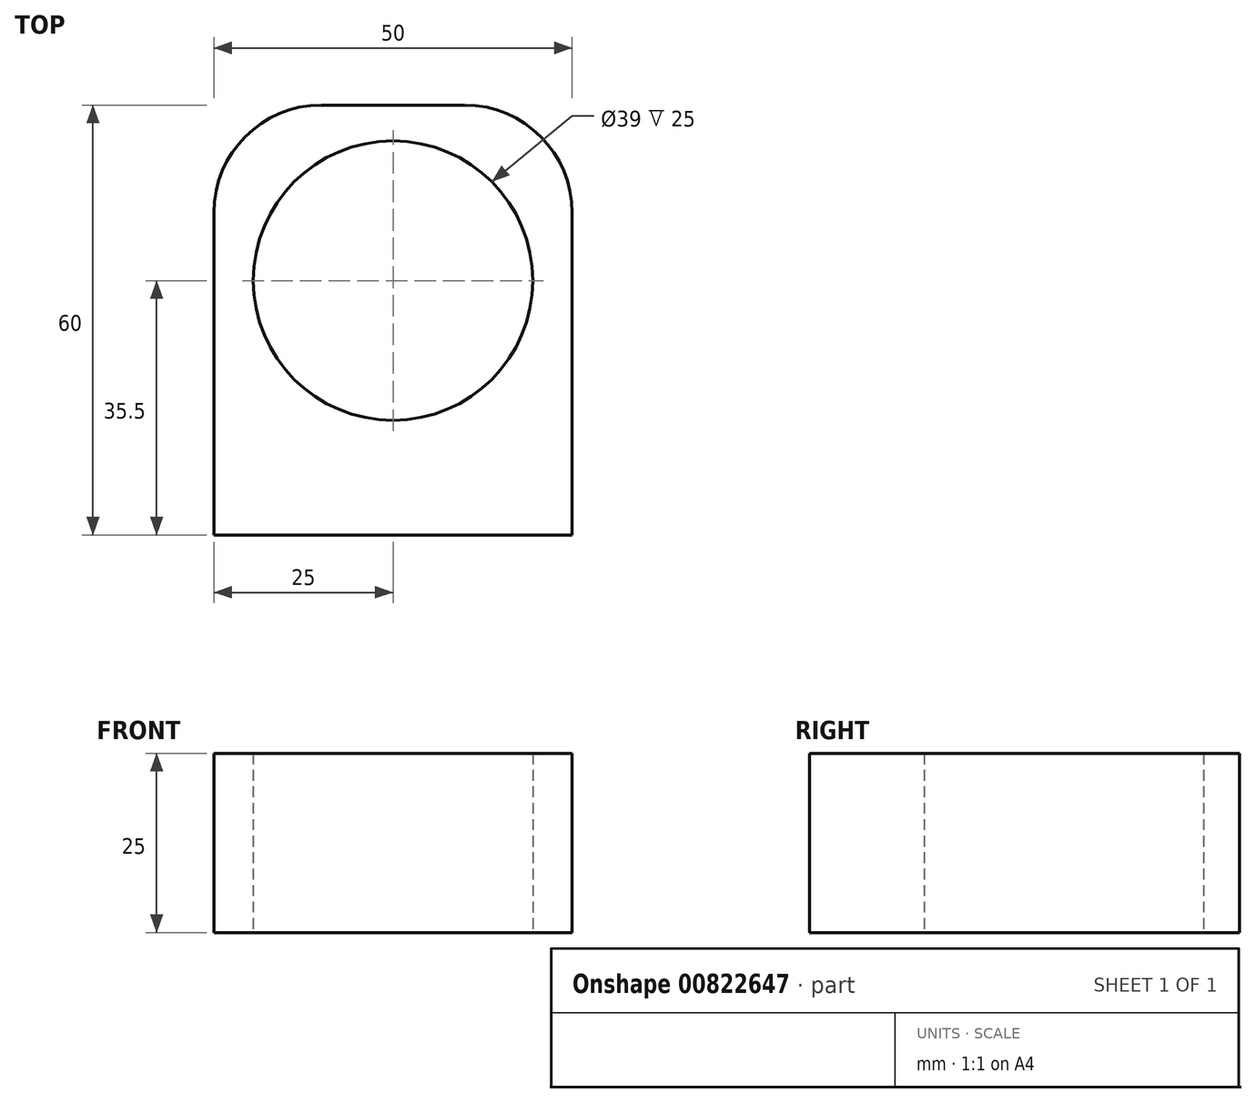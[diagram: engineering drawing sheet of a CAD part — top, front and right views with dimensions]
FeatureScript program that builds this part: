
annotation { "Feature Type Name" : "Feature", "Feature Type Description" : "" }
export const myFeature = defineFeature(function(context is Context, id is Id, definition is map)
    precondition{}
    {
        {
            var Q0;
            Q0=qCreatedBy(makeId("Top.planeOp"),FACE);
            var sketch = newSketch(context, id + "F0", { "sketchPlane" : qUnion([Q0])});
            skLineSegment(sketch, "E0.bottom", {"start": v(25, -30) * mm, "end": v(-25, -30) * mm});
            skLineSegment(sketch, "E0.top", {"start": v(25, 30) * mm, "end": v(-25, 30) * mm});
            skLineSegment(sketch, "E0.left", {"start": v(25, -30) * mm, "end": v(25, 30) * mm});
            skLineSegment(sketch, "E0.right", {"start": v(-25, -30) * mm, "end": v(-25, 30) * mm});
            skPoint(sketch, "E0.middle", {"position": v(0, 0) * mm});
            skPoint(sketch, "E1", {"position": v(0, 5.5) * mm});
            skCircle(sketch, "E2", {"center": v(0, 5.5) * mm, "radius": 19.5 * mm});
            skSolve(sketch);
        }
        {
            var Q0;
            Q0=makeQuery(id+"F0.imprint","IMPRINT",FACE,{"disambiguationData":[TD([[makeQuery(id+"F0.imprint","IMPRINT",EDGE,{"derivedFrom":sQuery(id+"F0.wireOp",EDGE,"E0.bottom")}),-1.0]])]});
            extrude(context, id + "F1", {"entities" : qUnion([Q0]), "depth" : 25 * mm, "offsetDistance" : 25 * mm});
        }
        {
            var Q0;
            Q0=makeQuery(id+"F1.opExtrude","SWEPT_EDGE",EDGE,{"disambiguationData":[OSD([sQuery(id+"F0.wireOp",EDGE,"E0.top"),sQuery(id+"F0.wireOp",EDGE,"E0.right")])]});
            fillet(context, id + "F2", {"entities" : qUnion([Q0]), "radius" : 15 * mm, "tangentPropagation" : true, "allowEdgeOverflow" : false});
        }
        {
            var Q0;
            Q0=makeQuery(id+"F1.opExtrude","SWEPT_EDGE",EDGE,{"disambiguationData":[OSD([sQuery(id+"F0.wireOp",EDGE,"E0.top"),sQuery(id+"F0.wireOp",EDGE,"E0.right")])]});
            var Q1;
            Q1=makeQuery(id+"F1.opExtrude","SWEPT_EDGE",EDGE,{"disambiguationData":[OSD([sQuery(id+"F0.wireOp",EDGE,"E0.top"),sQuery(id+"F0.wireOp",EDGE,"E0.left")])]});
            fillet(context, id + "F3", {"entities" : qUnion([Q0, Q1]), "radius" : 15 * mm, "tangentPropagation" : true, "allowEdgeOverflow" : false});
        }
    });
